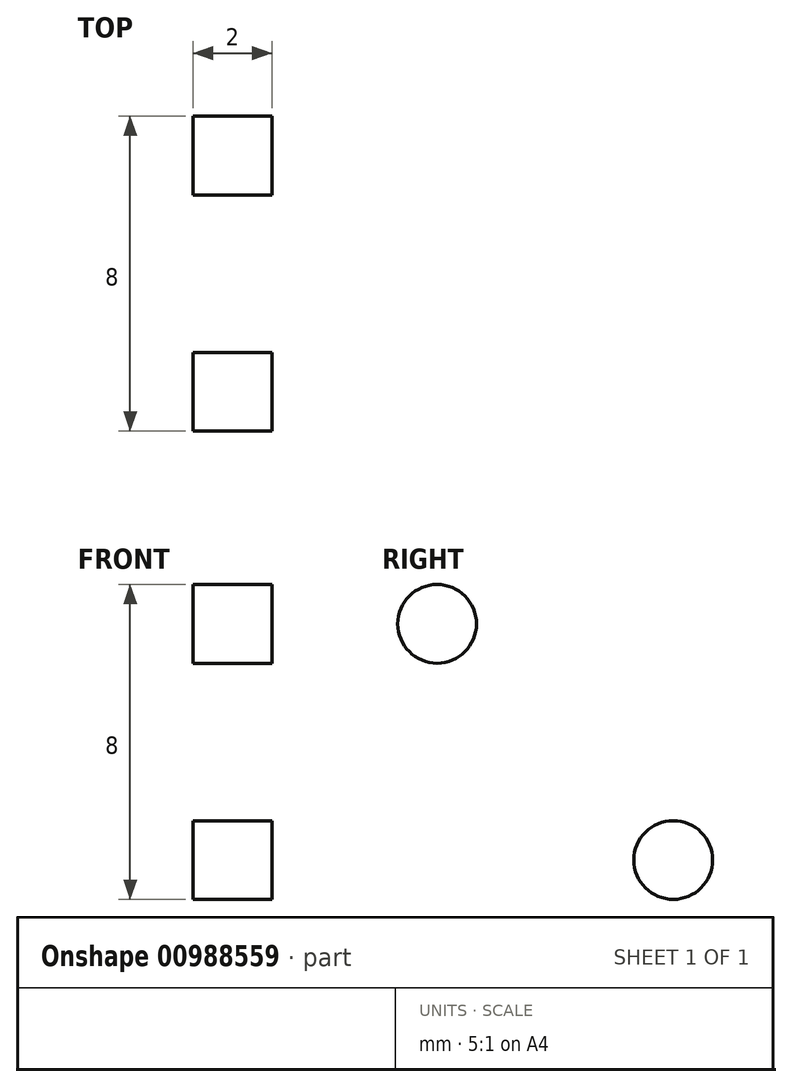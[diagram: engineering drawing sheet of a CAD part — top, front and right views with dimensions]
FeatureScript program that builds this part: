
annotation { "Feature Type Name" : "Feature", "Feature Type Description" : "" }
export const myFeature = defineFeature(function(context is Context, id is Id, definition is map)
    precondition{}
    {
        {
            var Q0;
            Q0=qCreatedBy(makeId("Top.planeOp"),FACE);
            var sketch = newSketch(context, id + "F0", { "sketchPlane" : qUnion([Q0])});
            skLineSegment(sketch, "E0.bottom", {"start": v(-10.29, -39.42) * mm, "end": v(-8.29, -39.42) * mm});
            skLineSegment(sketch, "E0.top", {"start": v(-10.29, -49.42) * mm, "end": v(-8.29, -49.42) * mm});
            skLineSegment(sketch, "E0.left", {"start": v(-10.29, -39.42) * mm, "end": v(-10.29, -49.42) * mm});
            skLineSegment(sketch, "E0.right", {"start": v(-8.29, -39.42) * mm, "end": v(-8.29, -49.42) * mm});
            skSolve(sketch);
        }
        {
            var Q0;
            Q0 = qSketchRegion(id + "F0", true);
            extrude(context, id + "F1", {"entities" : qUnion([Q0]), "depth" : 10 * mm, "offsetDistance" : 25 * mm});
        }
        {
            var Q0;
            Q0=makeQuery(id+"F1.opExtrude","SWEPT_FACE",FACE,{"disambiguationData":[OSD([sQuery(id+"F0.wireOp",EDGE,"E0.left")])]});
            var sketch = newSketch(context, id + "F2", { "sketchPlane" : qUnion([Q0])});
            skLineSegment(sketch, "E1", {"start": v(44.42, 10) * mm, "end": v(44.42, 0) * mm, "construction": true});
            skLineSegment(sketch, "E2", {"start": v(39.42, 5) * mm, "end": v(49.42, 5) * mm, "construction": true});
            skCircle(sketch, "E3", {"center": v(41.42, 8) * mm, "radius": 1 * mm});
            skCircle(sketch, "E4.MirrorC", {"center": v(47.42, 8) * mm, "radius": 1 * mm});
            skCircle(sketch, "E5.MirrorC", {"center": v(47.42, 2) * mm, "radius": 1 * mm});
            skCircle(sketch, "E6.MirrorC", {"center": v(41.42, 2) * mm, "radius": 1 * mm});
            skCircle(sketch, "E7", {"center": v(44.42, 5) * mm, "radius": 1 * mm});
            skSolve(sketch);
        }
        {
            var Q0;
            Q0=makeQuery(id+"F2.imprint","IMPRINT",FACE,{"disambiguationData":[TD([[makeQuery(id+"F2.imprint","IMPRINT",EDGE,{"derivedFrom":sQuery(id+"F2.wireOp",EDGE,"E3")}),1.0]])]});
            var Q1;
            Q1=makeQuery(id+"F2.imprint","IMPRINT",FACE,{"disambiguationData":[TD([[makeQuery(id+"F2.imprint","IMPRINT",EDGE,{"derivedFrom":sQuery(id+"F2.wireOp",EDGE,"E7")}),1.0]])]});
            var Q2;
            Q2=makeQuery(id+"F2.imprint","IMPRINT",FACE,{"disambiguationData":[TD([[makeQuery(id+"F2.imprint","IMPRINT",EDGE,{"derivedFrom":sQuery(id+"F2.wireOp",EDGE,"E4.MirrorC")}),-1.0]])]});
            var Q3;
            Q3=makeQuery(id+"F2.imprint","IMPRINT",FACE,{"disambiguationData":[TD([[makeQuery(id+"F2.imprint","IMPRINT",EDGE,{"derivedFrom":sQuery(id+"F2.wireOp",EDGE,"E5.MirrorC")}),1.0]])]});
            var Q4;
            Q4=makeQuery(id+"F2.imprint","IMPRINT",FACE,{"disambiguationData":[TD([[makeQuery(id+"F2.imprint","IMPRINT",EDGE,{"derivedFrom":sQuery(id+"F2.wireOp",EDGE,"E6.MirrorC")}),-1.0]])]});
            extrude(context, id + "F3", {"entities" : qUnion([Q0, Q1, Q2, Q3, Q4]), "operationType" : NewBodyOperationType.REMOVE, "oppositeDirection" : true, "depth" : 3 * mm, "offsetDistance" : 25 * mm});
        }
    });
